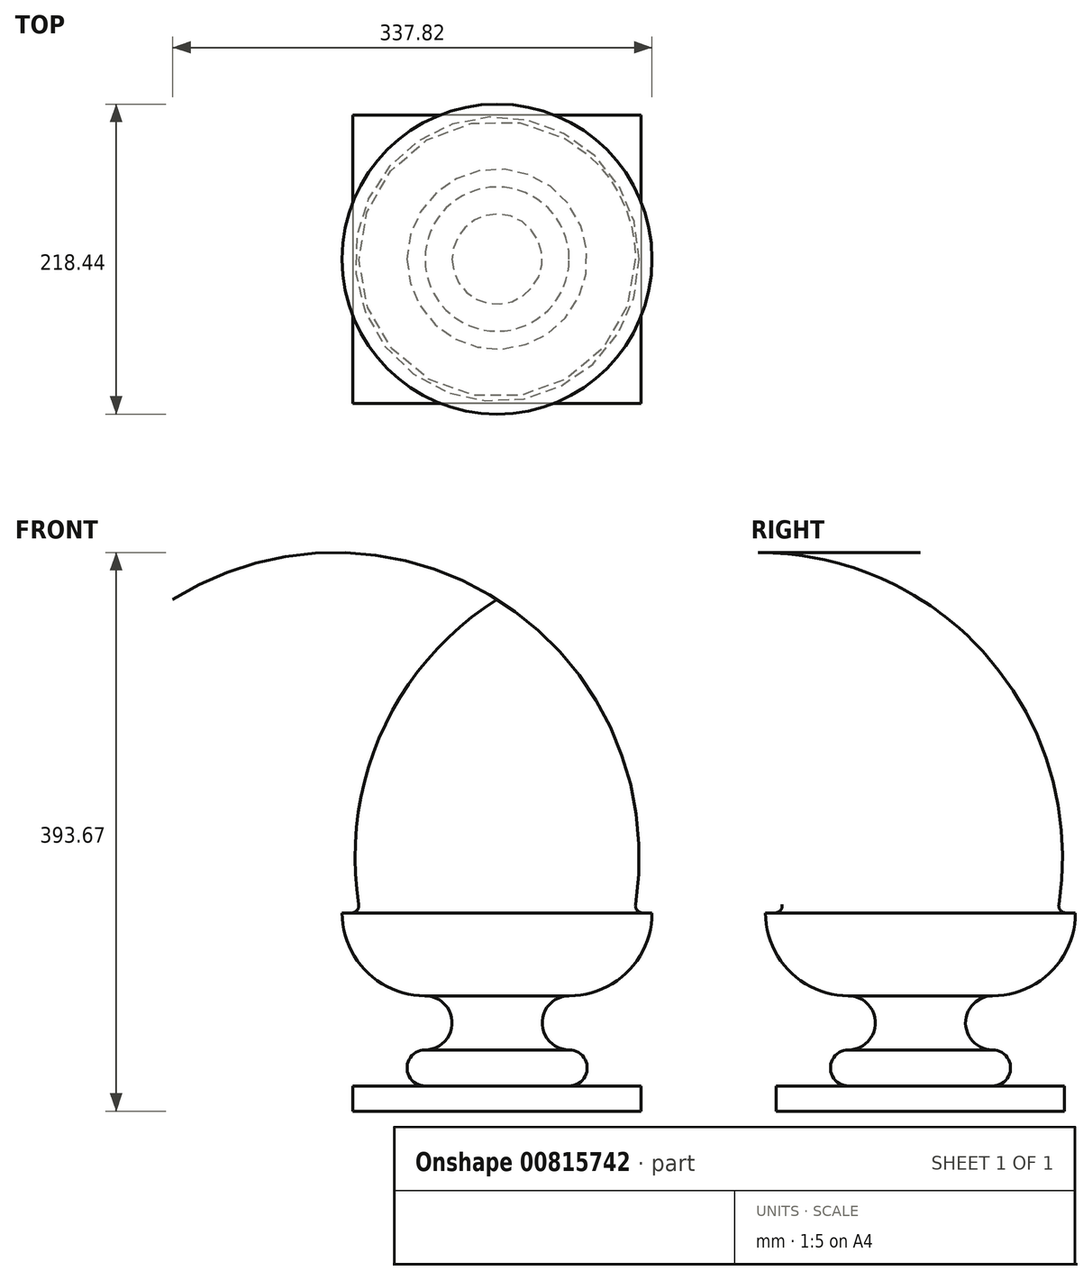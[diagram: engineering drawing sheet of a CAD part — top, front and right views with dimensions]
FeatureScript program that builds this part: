
annotation { "Feature Type Name" : "Feature", "Feature Type Description" : "" }
export const myFeature = defineFeature(function(context is Context, id is Id, definition is map)
    precondition{}
    {
        {
            var Q0;
            Q0=qCreatedBy(makeId("Top.planeOp"),FACE);
            var sketch = newSketch(context, id + "F0", { "sketchPlane" : qUnion([Q0])});
            skLineSegment(sketch, "E0.bottom", {"start": v(101.6, 101.6) * mm, "end": v(-101.6, 101.6) * mm});
            skLineSegment(sketch, "E0.top", {"start": v(101.6, -101.6) * mm, "end": v(-101.6, -101.6) * mm});
            skLineSegment(sketch, "E0.left", {"start": v(101.6, 101.6) * mm, "end": v(101.6, -101.6) * mm});
            skLineSegment(sketch, "E0.right", {"start": v(-101.6, 101.6) * mm, "end": v(-101.6, -101.6) * mm});
            skPoint(sketch, "E0.middle", {"position": v(0, 0) * mm});
            skSolve(sketch);
        }
        {
            var Q0;
            Q0=makeQuery(id+"F0.imprint","IMPRINT",FACE,{"disambiguationData":[TD([[makeQuery(id+"F0.imprint","IMPRINT",EDGE,{"derivedFrom":sQuery(id+"F0.wireOp",EDGE,"E0.bottom")}),1.0]])]});
            extrude(context, id + "F1", {"entities" : qUnion([Q0]), "depth" : 17.78 * mm, "offsetDistance" : 25.4 * mm});
        }
        {
            var Q0;
            Q0=qCreatedBy(makeId("Front.planeOp"),FACE);
            var sketch = newSketch(context, id + "F2", { "sketchPlane" : qUnion([Q0])});
            skLineSegment(sketch, "E1", {"start": v(0, 17.78) * mm, "end": v(0, 360.68) * mm});
            skArc(sketch, "E2", {"start": v(50.8, 81.28) * mm, "mid": v(92.1, 98.4) * mm, "end": v(109.22, 139.7) * mm});
            skArc(sketch, "E3", {"start": v(96.52, 139.7) * mm, "mid": v(82.25, 265.04) * mm, "end": v(0, 360.68) * mm});
            skLineSegment(sketch, "E4", {"start": v(109.22, 139.7) * mm, "end": v(96.52, 139.7) * mm});
            skArc(sketch, "E5", {"start": v(50.8, 17.78) * mm, "mid": v(63.5, 30.48) * mm, "end": v(50.8, 43.18) * mm});
            skArc(sketch, "E6", {"start": v(50.8, 81.28) * mm, "mid": v(31.75, 62.23) * mm, "end": v(50.8, 43.18) * mm});
            skLineSegment(sketch, "E7", {"start": v(0, 17.78) * mm, "end": v(50.8, 17.78) * mm});
            skSolve(sketch);
        }
        {
            var Q0;
            Q0=makeQuery(id+"F2.imprint","IMPRINT",FACE,{"disambiguationData":[TD([[makeQuery(id+"F2.imprint","IMPRINT",EDGE,{"derivedFrom":sQuery(id+"F2.wireOp",EDGE,"qheOzhUk-vern-bjLo-rjXj-7yKcvOgFfaP4")}),1.0]])]});
            var Q1;
            Q1=makeQuery(id+"F2.imprint","IMPRINT",FACE,{"disambiguationData":[TD([[makeQuery(id+"F2.imprint","IMPRINT",EDGE,{"derivedFrom":sQuery(id+"F2.wireOp",EDGE,"E1")}),-1.0]])]});
            var Q2;
            Q2=sQuery(id+"F2.wireOp",EDGE,"E1");
            revolve(context, id + "F3", {"operationType" : NewBodyOperationType.ADD, "surfaceOperationType" : NewSurfaceOperationType.NEW, "entities" : qUnion([Q0, Q1]), "axis" : qUnion([Q2]), "revolveType" : RevolveType.FULL});
        }
        {
            var Q0;
            Q0=makeQuery(id+"F3.opRevolve","SWEPT_EDGE",EDGE,{"disambiguationData":[OSD([sQuery(id+"F2.wireOp",EDGE,"E3"),sQuery(id+"F2.wireOp",EDGE,"E4")])]});
            fillet(context, id + "F4", {"entities" : qUnion([Q0]), "radius" : 5.08 * mm, "tangentPropagation" : true, "allowEdgeOverflow" : false});
        }
    });
